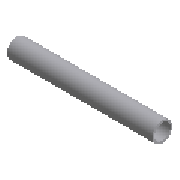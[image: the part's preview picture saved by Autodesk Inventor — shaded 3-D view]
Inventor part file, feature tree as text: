
AUTODESK INVENTOR PART (.ipt)
format: ipt  version: 2025 (Build 290162010, 162A)  size: 124,416 bytes
history: native  units: mm (DEFAULTED — no unit token found)
features: other x4, extrude x1
ambient origin geometry x8: Origin, YZ Plane, XZ Plane, XY Plane, X Axis, Y Axis, Z Axis, Center Point
bodies: Solid1 (feature_tree)
feature tree (5):
  extrude  "Extrusion1"  Depth=89.1mm
  other  "Work Axis1"
  other  "Work Point1"
  other  "Work Axis2"
  other  "Work Point2"
